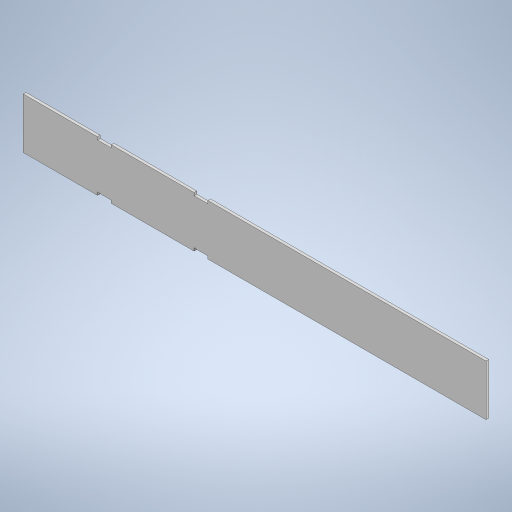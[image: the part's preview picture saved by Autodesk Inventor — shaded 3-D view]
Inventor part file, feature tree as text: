
AUTODESK INVENTOR PART (.ipt)
format: ipt  version: 2024 (Build 280153000, 153)  size: 336,384 bytes
history: native  units: mm
features: extrude x5, sketch x5, move_body x2, direct_edit x1
ambient origin geometry x8: Origin, YZ Plane, XZ Plane, XY Plane, X Axis, Y Axis, Z Axis, Center Point
bodies: Solid1 (feature_tree)
feature tree (13):
  extrude  "Extrusion1"  Depth=2.5mm TaperAngle=0.0deg
  direct_edit  "Direct Edit1"
  extrude  "Extrusion2"  Depth=10.0mm TaperAngle=0.0deg
  extrude  "Extrusion3"  Depth=100.0mm TaperAngle=0.0deg
  extrude  "Extrusion4"  [1 undecoded]
  extrude  "Extrusion5"  [1 undecoded]
  sketch  "Sketch1"  dims[d0=2.5mm d1=0.0mm d2=0.0mm d3=0.0mm d4=23.0mm]
  sketch  "Sketch2"  dims[d5=0.0mm d6=0.0mm d7=2.0mm d8=10.0mm d9=0.0mm]
  sketch  "Sketch4"  dims[d10=75.0mm d11=0.0mm d12=100.0mm d13=0.0mm]
  sketch  "Sketch5"  dims[d14=75.0mm d15=0.0mm]
  sketch  "Sketch6"
  move_body  "Move1"
  move_body  "Move2"
note: 2 required parameter values undecoded (feature->parameter linkage not recoverable at this tier; creation-order binding heuristic only, values carry confidence <= 0.55)
